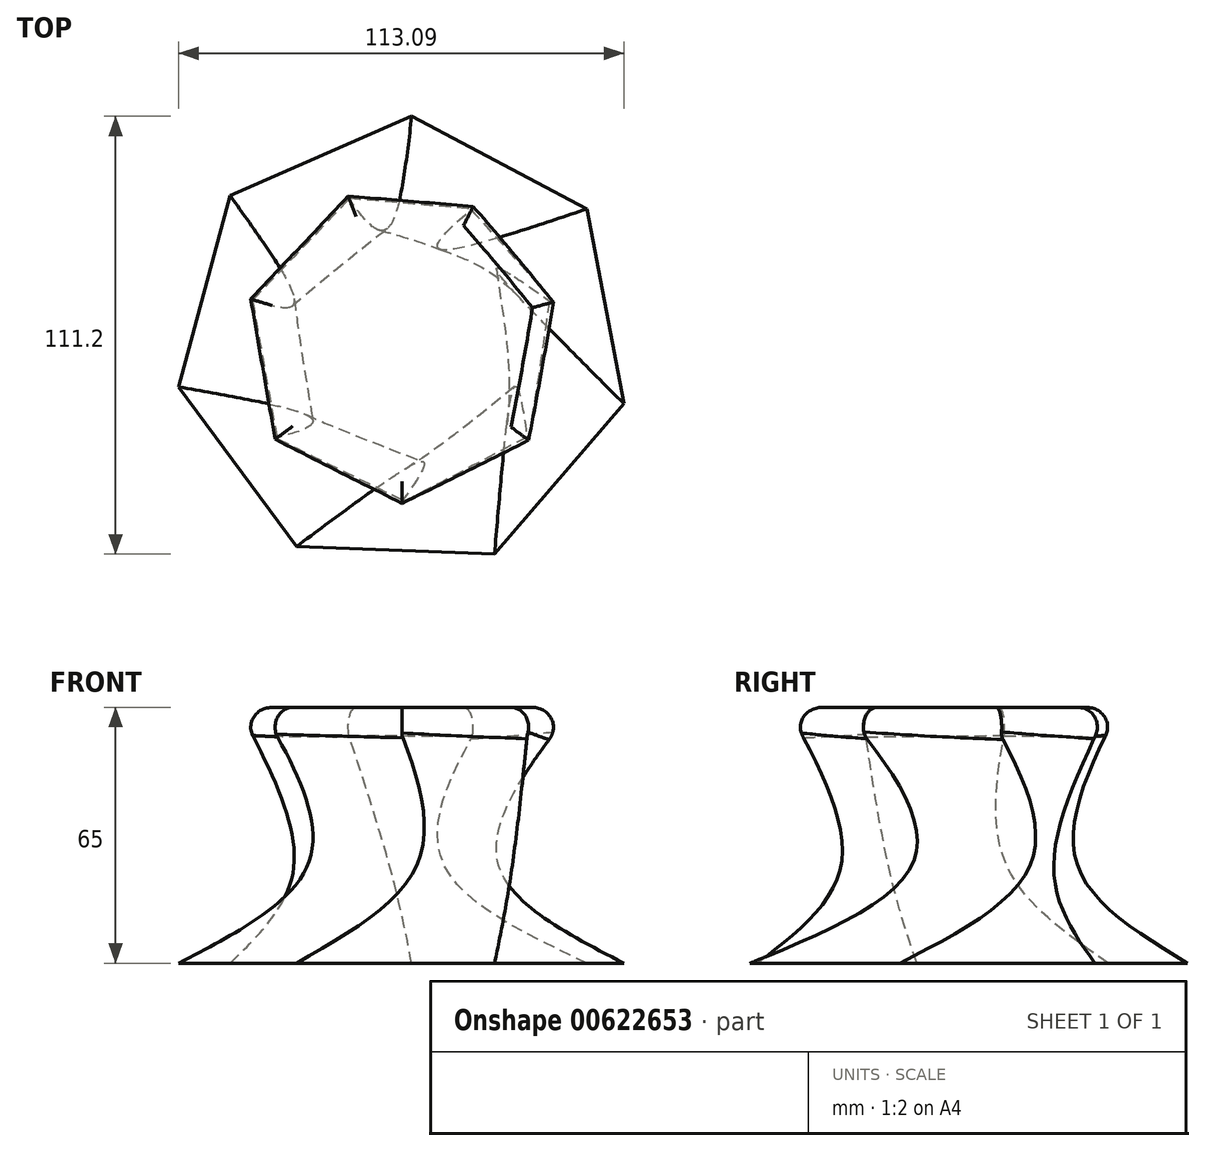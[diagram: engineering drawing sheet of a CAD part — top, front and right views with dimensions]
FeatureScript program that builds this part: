
annotation { "Feature Type Name" : "Feature", "Feature Type Description" : "" }
export const myFeature = defineFeature(function(context is Context, id is Id, definition is map)
    precondition{}
    {
        {
            var Q0;
            Q0=qCreatedBy(makeId("Top.planeOp"),FACE);
            var sketch = newSketch(context, id + "F0", { "sketchPlane" : qUnion([Q0])});
            skCircle(sketch, "E0.cCircle", {"center": v(0, 0) * mm, "radius": 52.3 * mm, "construction": true});
            skLineSegment(sketch, "E0.0", {"start": v(-57.03, -10.79) * mm, "end": v(-44, 37.86) * mm});
            skLineSegment(sketch, "E0.1", {"start": v(-44, 37.86) * mm, "end": v(2.17, 58) * mm});
            skLineSegment(sketch, "E0.2", {"start": v(2.17, 58) * mm, "end": v(46.7, 34.46) * mm});
            skLineSegment(sketch, "E0.3", {"start": v(46.7, 34.46) * mm, "end": v(56.06, -15.03) * mm});
            skLineSegment(sketch, "E0.4", {"start": v(56.06, -15.03) * mm, "end": v(23.2, -53.2) * mm});
            skLineSegment(sketch, "E0.5", {"start": v(23.2, -53.2) * mm, "end": v(-27.12, -51.32) * mm});
            skLineSegment(sketch, "E0.6", {"start": v(-27.12, -51.32) * mm, "end": v(-57.03, -10.79) * mm});
            skPoint(sketch, "E0.0.midPoint", {"position": v(-50.51, 13.54) * mm});
            skSolve(sketch);
        }
        {
            var Q0;
            Q0=qCreatedBy(makeId("Top.planeOp"),FACE);
            cPlane(context, id + "F1", {"entities" : qUnion([Q0]), "cplaneType" : CPlaneType.OFFSET, "offset" : 25 * mm, "width" : 150 * mm, "height" : 150 * mm});
        }
        {
            var Q0;
            Q0=qCreatedBy(id+"F1.planeOp",FACE);
            var sketch = newSketch(context, id + "F2", { "sketchPlane" : qUnion([Q0])});
            skCircle(sketch, "E1.cCircle", {"center": v(0, 0) * mm, "radius": 26.16 * mm, "construction": true});
            skLineSegment(sketch, "E1.0", {"start": v(-27.74, 11.96) * mm, "end": v(-3.51, 30) * mm});
            skLineSegment(sketch, "E1.1", {"start": v(-3.51, 30) * mm, "end": v(24.23, 18.04) * mm});
            skLineSegment(sketch, "E1.2", {"start": v(24.23, 18.04) * mm, "end": v(27.74, -11.96) * mm});
            skLineSegment(sketch, "E1.3", {"start": v(27.74, -11.96) * mm, "end": v(3.51, -30) * mm});
            skLineSegment(sketch, "E1.4", {"start": v(3.51, -30) * mm, "end": v(-24.23, -18.04) * mm});
            skLineSegment(sketch, "E1.5", {"start": v(-24.23, -18.04) * mm, "end": v(-27.74, 11.96) * mm});
            skPoint(sketch, "E1.0.midPoint", {"position": v(-15.62, 20.98) * mm});
            skSolve(sketch);
        }
        {
            var Q0;
            Q0=qCreatedBy(id+"F1.planeOp",FACE);
            cPlane(context, id + "F3", {"entities" : qUnion([Q0]), "cplaneType" : CPlaneType.OFFSET, "offset" : 40 * mm, "width" : 150 * mm, "height" : 150 * mm});
        }
        {
            var Q0;
            Q0=qCreatedBy(id+"F3.planeOp",FACE);
            var sketch = newSketch(context, id + "F4", { "sketchPlane" : qUnion([Q0])});
            skCircle(sketch, "E2.cCircle", {"center": v(0, 0) * mm, "radius": 39.5 * mm, "construction": true});
            skLineSegment(sketch, "E2.0", {"start": v(-41.94, 12.8) * mm, "end": v(-16.14, 40.77) * mm});
            skLineSegment(sketch, "E2.1", {"start": v(-16.14, 40.77) * mm, "end": v(21.8, 38.04) * mm});
            skLineSegment(sketch, "E2.2", {"start": v(21.8, 38.04) * mm, "end": v(43.34, 6.66) * mm});
            skLineSegment(sketch, "E2.3", {"start": v(43.34, 6.66) * mm, "end": v(32.23, -29.73) * mm});
            skLineSegment(sketch, "E2.4", {"start": v(32.23, -29.73) * mm, "end": v(-3.15, -43.73) * mm});
            skLineSegment(sketch, "E2.5", {"start": v(-3.15, -43.73) * mm, "end": v(-36.15, -24.8) * mm});
            skLineSegment(sketch, "E2.6", {"start": v(-36.15, -24.8) * mm, "end": v(-41.94, 12.8) * mm});
            skPoint(sketch, "E2.0.midPoint", {"position": v(-29.04, 26.78) * mm});
            skSolve(sketch);
        }
        {
            var Q0;
            Q0=makeQuery(id+"F0.imprint","IMPRINT",FACE,{"disambiguationData":[TD([[makeQuery(id+"F0.imprint","IMPRINT",EDGE,{"derivedFrom":sQuery(id+"F0.wireOp",EDGE,"E0.0")}),-1.0]])]});
            var Q1;
            Q1=makeQuery(id+"F2.imprint","IMPRINT",FACE,{"disambiguationData":[TD([[makeQuery(id+"F2.imprint","IMPRINT",EDGE,{"derivedFrom":sQuery(id+"F2.wireOp",EDGE,"E1.0")}),-1.0]])]});
            var Q2;
            Q2=makeQuery(id+"F4.imprint","IMPRINT",FACE,{"disambiguationData":[TD([[makeQuery(id+"F4.imprint","IMPRINT",EDGE,{"derivedFrom":sQuery(id+"F4.wireOp",EDGE,"E2.0")}),-1.0]])]});
            loft(context, id + "F5", {"sheetProfilesArray" : [{ "sheetProfileEntities" : qUnion([Q0]) }, { "sheetProfileEntities" : qUnion([Q1]) }, { "sheetProfileEntities" : qUnion([Q2]) }]});
        }
        {
            var Q0;
            Q0=makeQuery(id+"F5.opLoft","MID_CAP_EDGE",EDGE,{"disambiguationData":[OSD([sQuery(id+"F4.wireOp",EDGE,"E2.4"),sQuery(id+"F4.wireOp",EDGE,"E2.5"),sQuery(id+"F4.wireOp",EDGE,"E2.6")])],"capPos":2.0});
            var Q1;
            Q1=makeQuery(id+"F5.opLoft","MID_CAP_EDGE",EDGE,{"disambiguationData":[OSD([sQuery(id+"F4.wireOp",EDGE,"E2.0"),sQuery(id+"F4.wireOp",EDGE,"E2.5"),sQuery(id+"F4.wireOp",EDGE,"E2.6")])],"capPos":2.0});
            var Q2;
            Q2=makeQuery(id+"F5.opLoft","MID_CAP_EDGE",EDGE,{"disambiguationData":[OSD([sQuery(id+"F4.wireOp",EDGE,"E2.3"),sQuery(id+"F4.wireOp",EDGE,"E2.4"),sQuery(id+"F4.wireOp",EDGE,"E2.5")])],"capPos":2.0});
            var Q3;
            Q3=makeQuery(id+"F5.opLoft","MID_CAP_EDGE",EDGE,{"disambiguationData":[OSD([sQuery(id+"F4.wireOp",EDGE,"E2.2"),sQuery(id+"F4.wireOp",EDGE,"E2.3"),sQuery(id+"F4.wireOp",EDGE,"E2.4")])],"capPos":2.0});
            var Q4;
            Q4=makeQuery(id+"F5.opLoft","MID_CAP_EDGE",EDGE,{"disambiguationData":[OSD([sQuery(id+"F4.wireOp",EDGE,"E2.1"),sQuery(id+"F4.wireOp",EDGE,"E2.2"),sQuery(id+"F4.wireOp",EDGE,"E2.3")])],"capPos":2.0});
            var Q5;
            Q5=makeQuery(id+"F5.opLoft","MID_CAP_EDGE",EDGE,{"disambiguationData":[OSD([sQuery(id+"F4.wireOp",EDGE,"E2.0"),sQuery(id+"F4.wireOp",EDGE,"E2.1"),sQuery(id+"F4.wireOp",EDGE,"E2.2")])],"capPos":2.0});
            var Q6;
            Q6=makeQuery(id+"F5.opLoft","MID_CAP_EDGE",EDGE,{"disambiguationData":[OSD([sQuery(id+"F4.wireOp",EDGE,"E2.0"),sQuery(id+"F4.wireOp",EDGE,"E2.1"),sQuery(id+"F4.wireOp",EDGE,"E2.6")])],"capPos":2.0});
            fillet(context, id + "F6", {"entities" : qUnion([Q0, Q1, Q2, Q3, Q4, Q5, Q6]), "radius" : 5 * mm, "tangentPropagation" : true, "allowEdgeOverflow" : false});
        }
    });
